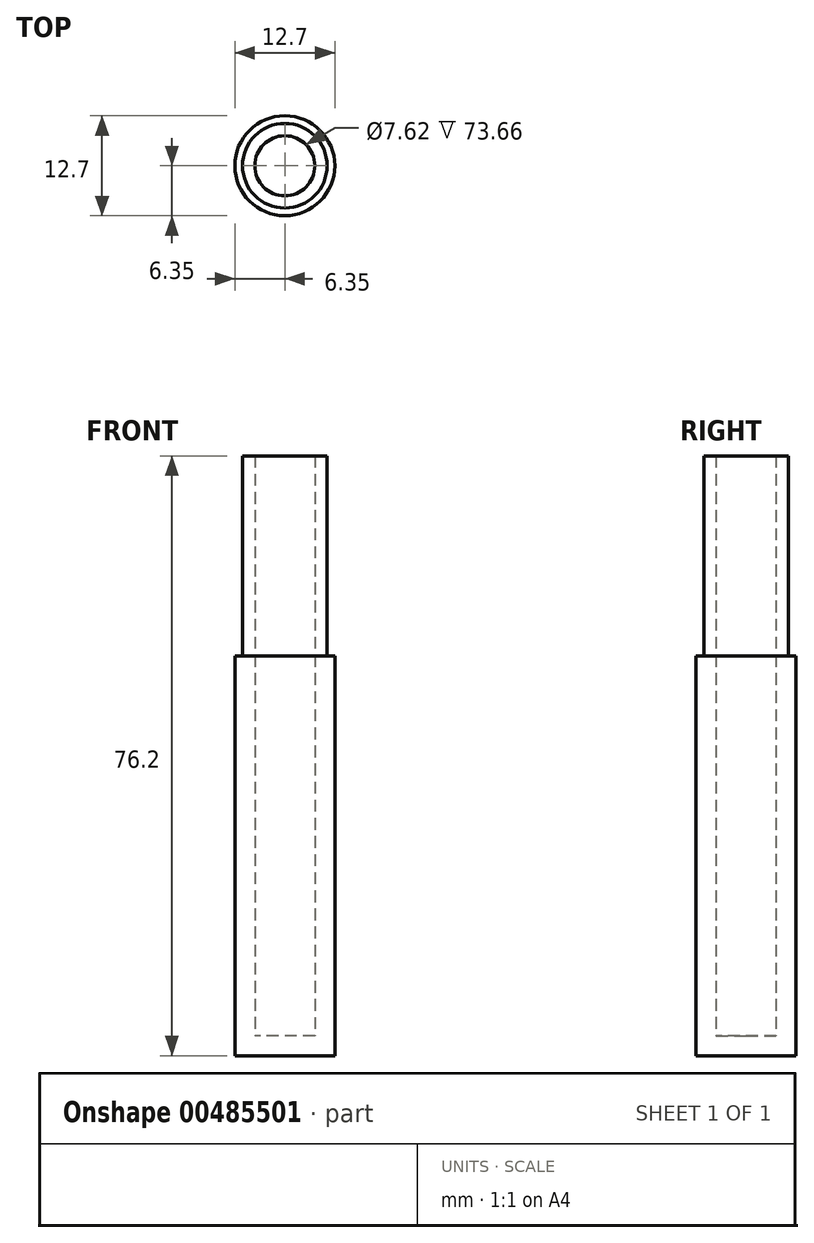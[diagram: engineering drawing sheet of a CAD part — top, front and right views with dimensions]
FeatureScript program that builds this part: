
annotation { "Feature Type Name" : "Feature", "Feature Type Description" : "" }
export const myFeature = defineFeature(function(context is Context, id is Id, definition is map)
    precondition{}
    {
        {
            var Q0;
            Q0=qCreatedBy(makeId("Top.planeOp"),FACE);
            var sketch = newSketch(context, id + "F0", { "sketchPlane" : qUnion([Q0])});
            skCircle(sketch, "E0", {"center": v(0, 0) * mm, "radius": 6.35 * mm});
            skSolve(sketch);
        }
        {
            var Q0;
            Q0 = qSketchRegion(id + "F0", true);
            extrude(context, id + "F1", {"entities" : qUnion([Q0]), "depth" : 76.2 * mm});
        }
        {
            var Q0;
            Q0=makeQuery(id+"F1.opExtrude","CAP_FACE",FACE,{"disambiguationData":[OSD([sQuery(id+"F0.wireOp",EDGE,"E0")])],"isStart":false});
            shell(context, id + "F2", {"entities" : qUnion([Q0]), "thickness" : 2.54 * mm});
        }
        {
            var Q0;
            Q0=makeQuery(id+"F1.opExtrude","CAP_FACE",FACE,{"disambiguationData":[OSD([sQuery(id+"F0.wireOp",EDGE,"E0")])],"isStart":false});
            var sketch = newSketch(context, id + "F3", { "sketchPlane" : qUnion([Q0])});
            skLineSegment(sketch, "E1", {"start": v(4.35, -4.62) * mm, "end": v(21.7, 14.84) * mm});
            skCircle(sketch, "E2", {"center": v(0, 0) * mm, "radius": 0.81 * mm});
            skSolve(sketch);
        }
        {
            var Q0;
            Q0=sQuery(id+"F3.wireOp",EDGE,"E2");
            extrude(context, id + "F4", {"bodyType" : ToolBodyType.SURFACE, "surfaceEntities" : qUnion([Q0]), "depth" : 25.4 * mm});
        }
        {
            var Q0;
            Q0=makeQuery(id+"F1.opExtrude","CAP_FACE",FACE,{"disambiguationData":[OSD([sQuery(id+"F0.wireOp",EDGE,"E0")])],"isStart":false});
            var sketch = newSketch(context, id + "F5", { "sketchPlane" : qUnion([Q0])});
            skCircle(sketch, "E3", {"center": v(0, 0) * mm, "radius": 5.37 * mm});
            skSolve(sketch);
        }
        {
            var Q0;
            Q0=makeQuery(id+"F5.imprint","IMPRINT",FACE,{"disambiguationData":[TD([[makeQuery(id+"F5.imprint","IMPRINT",EDGE,{"derivedFrom":sQuery(id+"F5.wireOp",EDGE,"E3")}),-1.0]])]});
            extrude(context, id + "F6", {"entities" : qUnion([Q0]), "operationType" : NewBodyOperationType.REMOVE, "oppositeDirection" : true, "depth" : 25.4 * mm});
        }
    });
